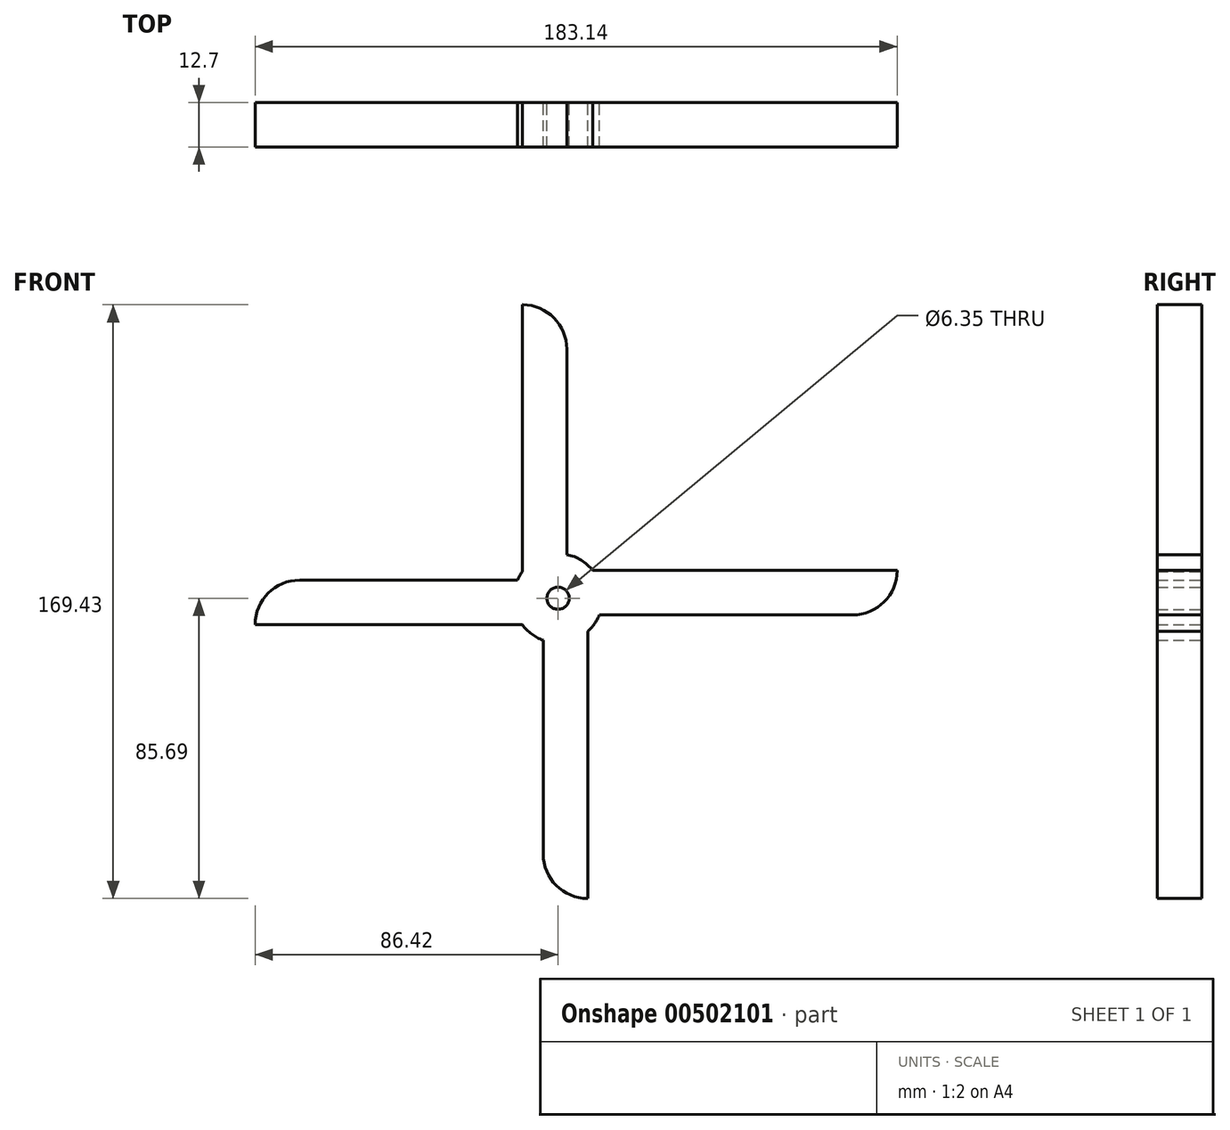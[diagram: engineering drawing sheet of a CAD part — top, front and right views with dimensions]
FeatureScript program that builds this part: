
annotation { "Feature Type Name" : "Feature", "Feature Type Description" : "" }
export const myFeature = defineFeature(function(context is Context, id is Id, definition is map)
    precondition{}
    {
        {
            var Q0;
            Q0=qCreatedBy(makeId("Front.planeOp"),FACE);
            var sketch = newSketch(context, id + "F0", { "sketchPlane" : qUnion([Q0])});
            skCircle(sketch, "E0", {"center": v(0, 0) * mm, "radius": 12.7 * mm});
            skCircle(sketch, "E1", {"center": v(0, 0) * mm, "radius": 3.18 * mm});
            skLineSegment(sketch, "E2", {"start": v(-10.22, 7.54) * mm, "end": v(-10.22, 83.74) * mm});
            skLineSegment(sketch, "E3", {"start": v(2.48, 12.46) * mm, "end": v(2.48, 71.04) * mm});
            skLineSegment(sketch, "E4", {"start": v(-10.22, 83.74) * mm, "end": v(-10.12, 83.74) * mm});
            skLineSegment(sketch, "E5", {"start": v(-4.26, -11.97) * mm, "end": v(-4.26, -72.99) * mm});
            skLineSegment(sketch, "E6", {"start": v(8.44, -9.5) * mm, "end": v(8.44, -85.7) * mm});
            skLineSegment(sketch, "E7", {"start": v(8.44, -85.7) * mm, "end": v(8.9, -85.68) * mm});
            skLineSegment(sketch, "E8", {"start": v(9.93, 7.92) * mm, "end": v(96.72, 7.92) * mm});
            skLineSegment(sketch, "E9", {"start": v(11.77, -4.78) * mm, "end": v(84.02, -4.78) * mm});
            skLineSegment(sketch, "E10", {"start": v(96.72, 7.92) * mm, "end": v(96.72, 7.92) * mm});
            skLineSegment(sketch, "E11", {"start": v(-11.6, 5.16) * mm, "end": v(-73.72, 5.16) * mm});
            skLineSegment(sketch, "E12", {"start": v(-10.22, -7.54) * mm, "end": v(-86.42, -7.54) * mm});
            skLineSegment(sketch, "E13", {"start": v(-86.42, -7.54) * mm, "end": v(-86.42, -7.52) * mm});
            skPoint(sketch, "E14.visualSharp", {"position": v(2.48, 83.64) * mm});
            skArc(sketch, "E14.filletArc", {"start": v(2.48, 71.04) * mm, "mid": v(-1.2, 79.99) * mm, "end": v(-10.12, 83.74) * mm});
            skPoint(sketch, "E15.visualSharp", {"position": v(96.72, -4.78) * mm});
            skArc(sketch, "E15.filletArc", {"start": v(84.02, -4.78) * mm, "mid": v(93, -1.06) * mm, "end": v(96.72, 7.92) * mm});
            skPoint(sketch, "E16.visualSharp", {"position": v(-4.26, -86.15) * mm});
            skArc(sketch, "E16.filletArc", {"start": v(-4.26, -72.99) * mm, "mid": v(-0.37, -82.13) * mm, "end": v(8.9, -85.68) * mm});
            skPoint(sketch, "E17.visualSharp", {"position": v(-86.4, 5.16) * mm});
            skArc(sketch, "E17.filletArc", {"start": v(-73.72, 5.16) * mm, "mid": v(-82.7, 1.45) * mm, "end": v(-86.42, -7.52) * mm});
            skSolve(sketch);
        }
        {
            var Q0;
            {var subQ1=sQuery(id+"F0.wireOp",EDGE,"E2");Q0=makeQuery(id+"F0.imprint","IMPRINT",FACE,{"disambiguationData":[TD([[makeQuery(id+"F0.imprint","IMPRINT",EDGE,{"derivedFrom":subQ1}),-1.0]])]});}
            var Q1;
            Q1=makeQuery(id+"F0.imprint","IMPRINT",FACE,{"disambiguationData":[TD([[makeQuery(id+"F0.imprint","IMPRINT",EDGE,{"derivedFrom":sQuery(id+"F0.wireOp",EDGE,"E1")}),-1.0]])]});
            var Q2;
            {var subQ1=sQuery(id+"F0.wireOp",EDGE,"E11");Q2=makeQuery(id+"F0.imprint","IMPRINT",FACE,{"disambiguationData":[TD([[makeQuery(id+"F0.imprint","IMPRINT",EDGE,{"derivedFrom":subQ1}),1.0]])]});}
            var Q3;
            {var subQ0=sQuery(id+"F0.wireOp",EDGE,"E5");Q3=makeQuery(id+"F0.imprint","IMPRINT",FACE,{"disambiguationData":[TD([[makeQuery(id+"F0.imprint","IMPRINT",EDGE,{"derivedFrom":subQ0}),1.0]])]});}
            var Q4;
            {var subQ0=sQuery(id+"F0.wireOp",EDGE,"E8");Q4=makeQuery(id+"F0.imprint","IMPRINT",FACE,{"disambiguationData":[TD([[makeQuery(id+"F0.imprint","IMPRINT",EDGE,{"derivedFrom":subQ0}),-1.0]])]});}
            extrude(context, id + "F1", {"entities" : qUnion([Q0, Q1, Q2, Q3, Q4]), "depth" : 12.7 * mm});
        }
    });
